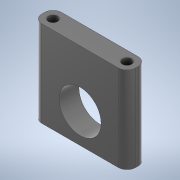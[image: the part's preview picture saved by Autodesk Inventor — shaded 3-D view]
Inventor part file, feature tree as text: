
AUTODESK INVENTOR PART (.ipt)
format: ipt  version: 2020 (Build 240168000, 168)  size: 151,552 bytes
history: native  units: mm
features: projected_geometry x6, sketch x3, extrude x2, other x1, fillet x1
ambient origin geometry x8: Origin, YZ Plane, XZ Plane, XY Plane, X Axis, Y Axis, Z Axis, Center Point
bodies: Body1 (feature_tree)
feature tree (13):
  other  "Твердое тело1"
  sketch  "Эскиз1"
  extrude  "Выдавливание1"  Depth=30.0mm
  fillet  "Сопряжение1"  Radius=3.8mm
  extrude  "Выдавливание2"  Depth=38.0mm
  sketch  "Эскиз2"
  sketch  "Эскиз3"
  projected_geometry  "Спроецированная петля1"
  projected_geometry  "Спроецированная петля2"
  projected_geometry  "Спроецированная петля3"
  projected_geometry  "Спроецированная петля4"
  projected_geometry  "Спроецированная петля5"
  projected_geometry  "Спроецированная петля6"
